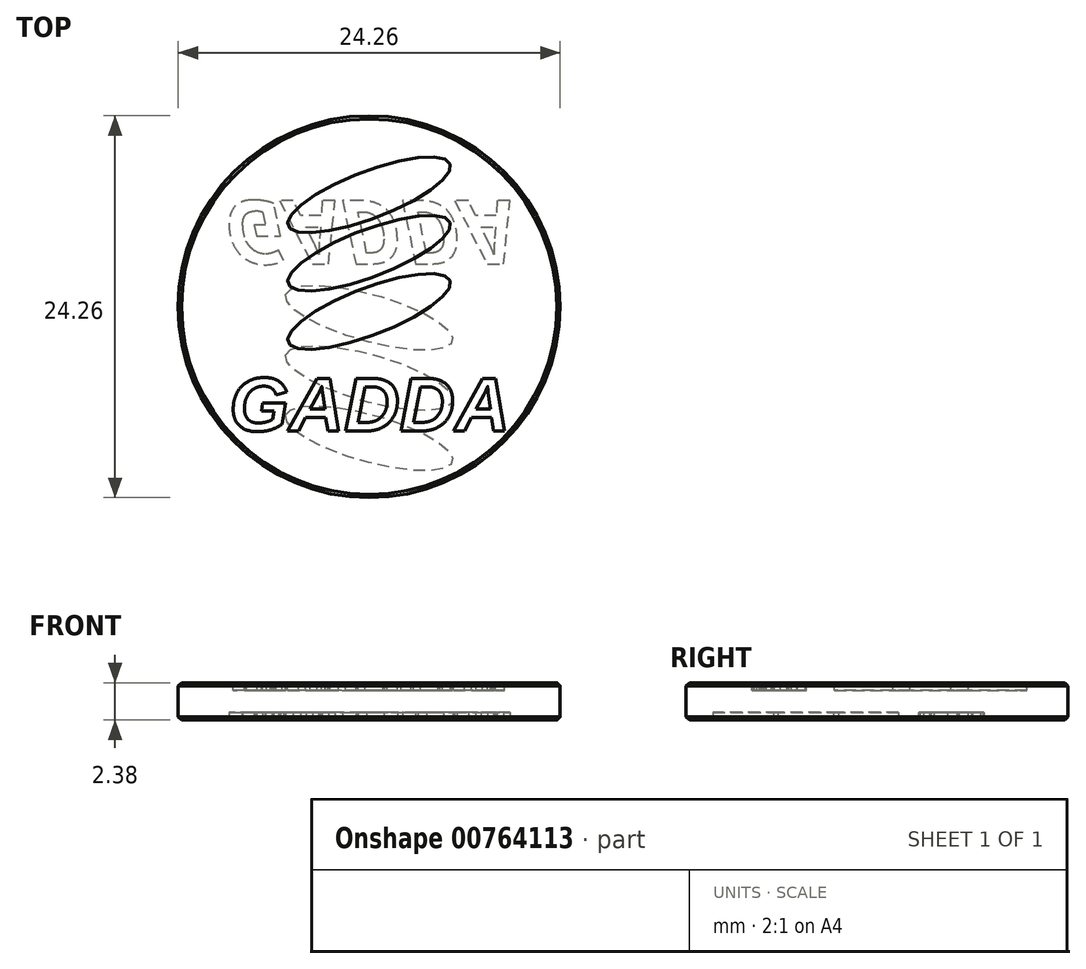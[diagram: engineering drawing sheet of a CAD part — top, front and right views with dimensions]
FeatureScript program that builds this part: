
annotation { "Feature Type Name" : "Feature", "Feature Type Description" : "" }
export const myFeature = defineFeature(function(context is Context, id is Id, definition is map)
    precondition{}
    {
        {
            assignVariable(context, id + "F0", {"name" : "S", "anyValue" : 2.38});
        }
        {
            var Q0;
            Q0=qCreatedBy(makeId("Top.planeOp"),FACE);
            var sketch = newSketch(context, id + "F1", { "sketchPlane" : qUnion([Q0])});
            skCircle(sketch, "E0", {"center": v(0, 0) * mm, "radius": 12.12 * mm});
            skSolve(sketch);
        }
        {
            var Q0;
            Q0 = qSketchRegion(id + "F1", true);
            extrude(context, id + "F2", {"entities" : qUnion([Q0]), "depth" : (getVariable(context, 'S')) * mm, "offsetDistance" : 25 * mm});
        }
        {
            var Q0;
            Q0=makeQuery(id+"F2.opExtrude","CAP_FACE",FACE,{"disambiguationData":[OSD([sQuery(id+"F1.wireOp",EDGE,"E0")])],"isStart":false});
            var Q1;
            Q1=makeQuery(id+"F2.opExtrude","CAP_EDGE",EDGE,{"disambiguationData":[OSD([sQuery(id+"F1.wireOp",EDGE,"E0")])],"isStart":true});
            chamfer(context, id + "F3", {"entities" : qUnion([Q0, Q1]), "width" : 0.2 * mm, "tangentPropagation" : true});
        }
        {
            var Q0;
            Q0=makeQuery(id+"F2.opExtrude","CAP_FACE",FACE,{"disambiguationData":[OSD([sQuery(id+"F1.wireOp",EDGE,"E0")])],"isStart":false});
            var sketch = newSketch(context, id + "F4", { "sketchPlane" : qUnion([Q0])});
            skEllipse(sketch, "E1", {"center": v(0, 7.1) * mm, "majorRadius": 5.5 * mm, "minorRadius": 1.5 * mm, "majorAxis": v(0.93, 0.36)});
            skEllipse(sketch, "E2.1.0.0", {"center": v(0, 3.4) * mm, "majorRadius": 5.5 * mm, "minorRadius": 1.5 * mm, "majorAxis": v(0.93, 0.36)});
            skEllipse(sketch, "E2.2.0.0", {"center": v(0, -0.3) * mm, "majorRadius": 5.5 * mm, "minorRadius": 1.5 * mm, "majorAxis": v(0.93, 0.36)});
            skText(sketch, "E3", { "text": "GADDA", "fontName": "Arimo-BoldItalic.ttf"});
            const initialGuessF4  = {"E3": [-0.00887, -0.00789, 1, 0, 0.0035]};
            skSetInitialGuess(sketch, initialGuessF4);
            skSolve(sketch);
        }
        {
            var Q0;
            Q0 = qSketchRegion(id + "F4", true);
            extrude(context, id + "F5", {"entities" : qUnion([Q0]), "operationType" : NewBodyOperationType.REMOVE, "oppositeDirection" : true, "depth" : 0.5 * mm, "offsetDistance" : 25 * mm});
        }
        {
            var Q0;
            Q0=makeQuery(id+"F2.opExtrude","CAP_FACE",FACE,{"disambiguationData":[OSD([sQuery(id+"F1.wireOp",EDGE,"E0")])],"isStart":true});
            var sketch = newSketch(context, id + "F6", { "sketchPlane" : qUnion([Q0])});
            skEllipse(sketch, "E4", {"center": v(0, 0.7) * mm, "majorRadius": 5.5 * mm, "minorRadius": 1.5 * mm, "majorAxis": v(-0.96, -0.27)});
            skEllipse(sketch, "E5.1.0.0", {"center": v(0, 4.53) * mm, "majorRadius": 5.5 * mm, "minorRadius": 1.5 * mm, "majorAxis": v(-0.96, -0.27)});
            skEllipse(sketch, "E5.2.0.0", {"center": v(0, 8.36) * mm, "majorRadius": 5.5 * mm, "minorRadius": 1.5 * mm, "majorAxis": v(-0.96, -0.27)});
            skLineSegment(sketch, "E5.direction1", {"start": v(0, 0.7) * mm, "end": v(0, 4.53) * mm, "construction": true});
            skText(sketch, "E6", { "text": "GADDA", "fontName": "OpenSans-BoldItalic.ttf"});
            const initialGuessF6  = {"E6": [-0.00923, -0.00673, 1, 0, 0.00404]};
            skSetInitialGuess(sketch, initialGuessF6);
            skSolve(sketch);
        }
        {
            var Q0;
            Q0 = qSketchRegion(id + "F6", true);
            extrude(context, id + "F7", {"entities" : qUnion([Q0]), "operationType" : NewBodyOperationType.REMOVE, "oppositeDirection" : true, "depth" : 0.5 * mm, "offsetDistance" : 25 * mm});
        }
    });
